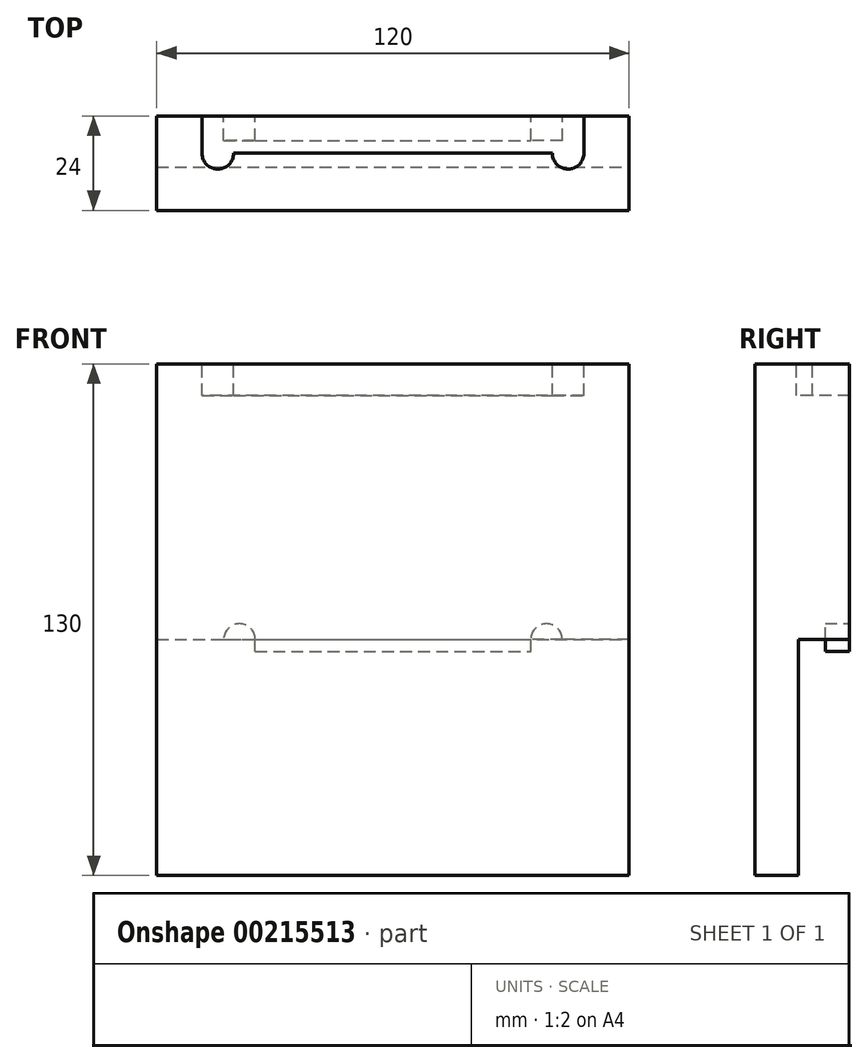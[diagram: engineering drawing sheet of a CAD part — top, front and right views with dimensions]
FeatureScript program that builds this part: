
annotation { "Feature Type Name" : "Feature", "Feature Type Description" : "" }
export const myFeature = defineFeature(function(context is Context, id is Id, definition is map)
    precondition{}
    {
        {
            var Q0;
            Q0=qCreatedBy(makeId("Top.planeOp"),FACE);
            var sketch = newSketch(context, id + "F0", { "sketchPlane" : qUnion([Q0])});
            skLineSegment(sketch, "E0.bottom", {"start": v(60, -12) * mm, "end": v(-60, -12) * mm});
            skLineSegment(sketch, "E0.top", {"start": v(60, 12) * mm, "end": v(-60, 12) * mm});
            skLineSegment(sketch, "E0.left", {"start": v(60, -12) * mm, "end": v(60, 12) * mm});
            skLineSegment(sketch, "E0.right", {"start": v(-60, -12) * mm, "end": v(-60, 12) * mm});
            skPoint(sketch, "E0.middle", {"position": v(0, 0) * mm});
            skSolve(sketch);
        }
        {
            var Q0;
            Q0 = qSketchRegion(id + "F0", true);
            extrude(context, id + "F1", {"entities" : qUnion([Q0]), "depth" : 130 * mm});
        }
        {
            var Q0;
            Q0=makeQuery(id+"F1.opExtrude","CAP_FACE",FACE,{"disambiguationData":[OSD([sQuery(id+"F0.wireOp",EDGE,"E0.bottom"),sQuery(id+"F0.wireOp",EDGE,"E0.top"),sQuery(id+"F0.wireOp",EDGE,"E0.left"),sQuery(id+"F0.wireOp",EDGE,"E0.right")])],"isStart":false});
            var sketch = newSketch(context, id + "F2", { "sketchPlane" : qUnion([Q0])});
            skLineSegment(sketch, "E1.bottom", {"start": v(-48.5, 12) * mm, "end": v(48.5, 12) * mm});
            skLineSegment(sketch, "E1.left", {"start": v(-48.5, 12) * mm, "end": v(-48.5, 2.5) * mm});
            skLineSegment(sketch, "E1.right", {"start": v(48.5, 12) * mm, "end": v(48.5, 2.5) * mm});
            skLineSegment(sketch, "E2", {"start": v(-48.5, 2.5) * mm, "end": v(48.5, 2.5) * mm});
            skSolve(sketch);
        }
        {
            var Q0;
            Q0 = qSketchRegion(id + "F2", true);
            extrude(context, id + "F3", {"entities" : qUnion([Q0]), "operationType" : NewBodyOperationType.REMOVE, "oppositeDirection" : true, "depth" : 8 * mm});
        }
        {
            var Q0;
            Q0=makeQuery(id+"F1.opExtrude","CAP_FACE",FACE,{"disambiguationData":[OSD([sQuery(id+"F0.wireOp",EDGE,"E0.bottom"),sQuery(id+"F0.wireOp",EDGE,"E0.top"),sQuery(id+"F0.wireOp",EDGE,"E0.left"),sQuery(id+"F0.wireOp",EDGE,"E0.right")])],"isStart":false});
            var sketch = newSketch(context, id + "F4", { "sketchPlane" : qUnion([Q0])});
            skLineSegment(sketch, "E3", {"start": v(-48.5, 2.5) * mm, "end": v(-40.5, 2.5) * mm});
            skLineSegment(sketch, "E4", {"start": v(0, 12.39) * mm, "end": v(0, -12) * mm, "construction": true});
            skArc(sketch, "E5", {"start": v(-48.5, 2.5) * mm, "mid": v(-44.5, -1.5) * mm, "end": v(-40.5, 2.5) * mm});
            skArc(sketch, "E6.MirrorCS", {"start": v(48.5, 2.5) * mm, "mid": v(44.5, -1.5) * mm, "end": v(40.5, 2.5) * mm});
            skLineSegment(sketch, "E7.MirrorCS", {"start": v(48.5, 2.5) * mm, "end": v(40.5, 2.5) * mm});
            skSolve(sketch);
        }
        {
            var Q0;
            Q0 = qSketchRegion(id + "F4", true);
            var Q1;
            Q1=makeQuery(id+"F3.boolean.opBoolean","COPY",FACE,{"derivedFrom":makeQuery(id+"F3.opExtrude","CAP_FACE",FACE,{"disambiguationData":[OSD([sQuery(id+"F2.wireOp",EDGE,"E1.bottom"),sQuery(id+"F2.wireOp",EDGE,"E1.left"),sQuery(id+"F2.wireOp",EDGE,"E1.right"),sQuery(id+"F2.wireOp",EDGE,"E2")])],"isStart":false})});
            extrude(context, id + "F5", {"entities" : qUnion([Q0]), "operationType" : NewBodyOperationType.REMOVE, "endBound" : BoundingType.UP_TO_SURFACE, "oppositeDirection" : true, "endBoundEntityFace" : qUnion([Q1]), "depth" : 25 * mm});
        }
        {
            var Q0;
            Q0=makeQuery(id+"F1.opExtrude","SWEPT_FACE",FACE,{"disambiguationData":[OSD([sQuery(id+"F0.wireOp",EDGE,"E0.left")])]});
            var sketch = newSketch(context, id + "F6", { "sketchPlane" : qUnion([Q0])});
            skLineSegment(sketch, "E8.bottom", {"start": v(12, 0) * mm, "end": v(-1, 0) * mm});
            skLineSegment(sketch, "E8.top", {"start": v(5.8, 60) * mm, "end": v(-1, 60) * mm});
            skLineSegment(sketch, "E8.left", {"start": v(12, 0) * mm, "end": v(12, 57) * mm});
            skLineSegment(sketch, "E8.right", {"start": v(-1, 0) * mm, "end": v(-1, 60) * mm});
            skLineSegment(sketch, "E9", {"start": v(5.8, 60) * mm, "end": v(5.8, 57) * mm});
            skLineSegment(sketch, "E10", {"start": v(5.8, 57) * mm, "end": v(12, 57) * mm});
            skSolve(sketch);
        }
        {
            var Q0;
            Q0 = qSketchRegion(id + "F6", true);
            extrude(context, id + "F7", {"entities" : qUnion([Q0]), "operationType" : NewBodyOperationType.REMOVE, "endBound" : BoundingType.THROUGH_ALL, "oppositeDirection" : true, "depth" : 25 * mm});
        }
        {
            var Q0;
            Q0=makeQuery(id+"F1.opExtrude","SWEPT_FACE",FACE,{"disambiguationData":[OSD([sQuery(id+"F0.wireOp",EDGE,"E0.top")])]});
            var sketch = newSketch(context, id + "F8", { "sketchPlane" : qUnion([Q0])});
            skLineSegment(sketch, "E11.bottom", {"start": v(-60, 57) * mm, "end": v(-35, 57) * mm});
            skLineSegment(sketch, "E11.top", {"start": v(-60, 60) * mm, "end": v(-35, 60) * mm});
            skLineSegment(sketch, "E11.left", {"start": v(-60, 57) * mm, "end": v(-60, 60) * mm});
            skLineSegment(sketch, "E11.right", {"start": v(-35, 57) * mm, "end": v(-35, 60) * mm});
            skLineSegment(sketch, "E12.bottom", {"start": v(60, 57) * mm, "end": v(35, 57) * mm});
            skLineSegment(sketch, "E12.top", {"start": v(60, 60) * mm, "end": v(35, 60) * mm});
            skLineSegment(sketch, "E12.left", {"start": v(60, 57) * mm, "end": v(60, 60) * mm});
            skLineSegment(sketch, "E12.right", {"start": v(35, 57) * mm, "end": v(35, 60) * mm});
            skSolve(sketch);
        }
        {
            var Q0;
            Q0 = qSketchRegion(id + "F8", true);
            var Q1;
            Q1=makeQuery(id+"F7.boolean.opBoolean","COPY",FACE,{"derivedFrom":makeQuery(id+"F7.opExtrude","SWEPT_FACE",FACE,{"disambiguationData":[OSD([sQuery(id+"F6.wireOp",EDGE,"E8.right")])]})});
            extrude(context, id + "F9", {"entities" : qUnion([Q0]), "operationType" : NewBodyOperationType.REMOVE, "endBound" : BoundingType.UP_TO_SURFACE, "oppositeDirection" : true, "endBoundEntityFace" : qUnion([Q1]), "depth" : 25 * mm});
        }
        {
            var Q0;
            Q0=makeQuery(id+"F1.opExtrude","SWEPT_FACE",FACE,{"disambiguationData":[OSD([sQuery(id+"F0.wireOp",EDGE,"E0.top")])]});
            var sketch = newSketch(context, id + "F10", { "sketchPlane" : qUnion([Q0])});
            skLineSegment(sketch, "E13", {"start": v(-35, 60) * mm, "end": v(-43, 60) * mm});
            skArc(sketch, "E14", {"start": v(-35, 60) * mm, "mid": v(-39, 64) * mm, "end": v(-43, 60) * mm});
            skLineSegment(sketch, "E15.MirrorCS", {"start": v(35, 60) * mm, "end": v(43, 60) * mm});
            skArc(sketch, "E16.MirrorCS", {"start": v(35, 60) * mm, "mid": v(39, 64) * mm, "end": v(43, 60) * mm});
            skSolve(sketch);
        }
        {
            var Q0;
            Q0 = qSketchRegion(id + "F10", true);
            var Q1;
            Q1=makeQuery(id+"F7.boolean.opBoolean","COPY",FACE,{"derivedFrom":makeQuery(id+"F7.opExtrude","SWEPT_FACE",FACE,{"disambiguationData":[OSD([sQuery(id+"F6.wireOp",EDGE,"E9")])]})});
            extrude(context, id + "F11", {"entities" : qUnion([Q0]), "operationType" : NewBodyOperationType.REMOVE, "endBound" : BoundingType.UP_TO_SURFACE, "oppositeDirection" : true, "endBoundEntityFace" : qUnion([Q1]), "depth" : 25 * mm});
        }
    });
